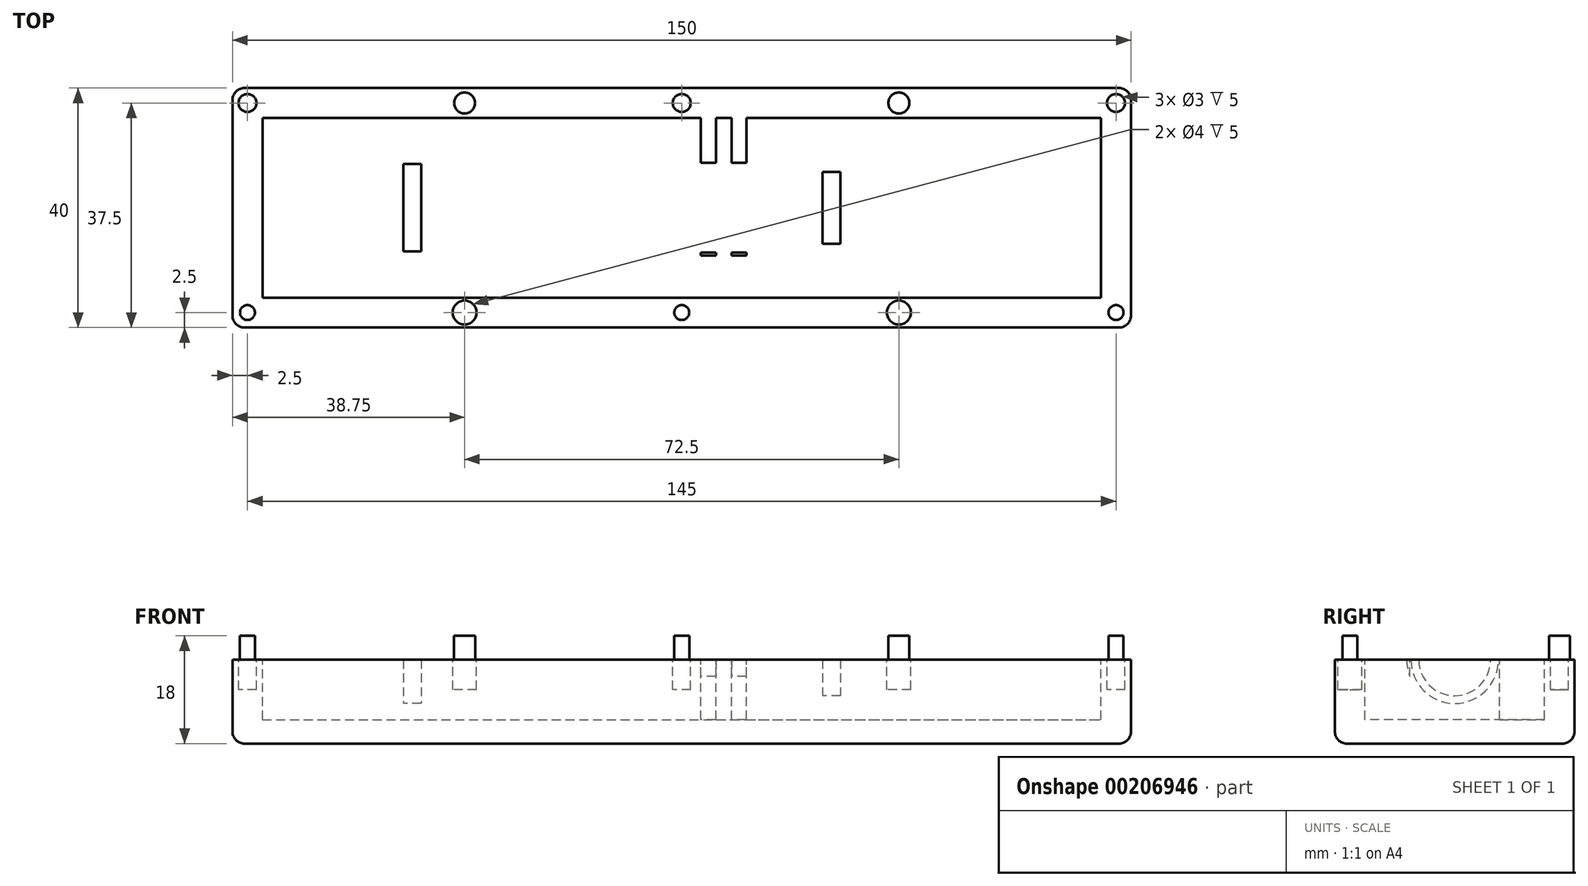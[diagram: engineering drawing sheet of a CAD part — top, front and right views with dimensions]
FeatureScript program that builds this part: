
annotation { "Feature Type Name" : "Feature", "Feature Type Description" : "" }
export const myFeature = defineFeature(function(context is Context, id is Id, definition is map)
    precondition{}
    {
        {
            var Q0;
            Q0=qCreatedBy(makeId("Top.planeOp"),FACE);
            var sketch = newSketch(context, id + "F0", { "sketchPlane" : qUnion([Q0])});
            skLineSegment(sketch, "E0.bottom", {"start": v(-70, 15) * mm, "end": v(70, 15) * mm});
            skLineSegment(sketch, "E0.top", {"start": v(-70, -15) * mm, "end": v(70, -15) * mm});
            skLineSegment(sketch, "E0.left", {"start": v(-70, 15) * mm, "end": v(-70, -15) * mm});
            skLineSegment(sketch, "E0.right", {"start": v(70, 15) * mm, "end": v(70, -15) * mm});
            skPoint(sketch, "E0.middle", {"position": v(0, 0) * mm});
            skLineSegment(sketch, "E1.bottom", {"start": v(3.2, 15) * mm, "end": v(10.8, 15) * mm});
            skLineSegment(sketch, "E1.top", {"start": v(3.2, -15) * mm, "end": v(10.8, -15) * mm});
            skLineSegment(sketch, "E1.left", {"start": v(3.2, 15) * mm, "end": v(3.2, -15) * mm});
            skLineSegment(sketch, "E1.right", {"start": v(10.8, 15) * mm, "end": v(10.8, -15) * mm});
            skPoint(sketch, "E1.middle", {"position": v(7, 0) * mm});
            skLineSegment(sketch, "E2.bottom", {"start": v(26.5, -8) * mm, "end": v(23.5, -8) * mm});
            skLineSegment(sketch, "E2.top", {"start": v(26.5, 8) * mm, "end": v(23.5, 8) * mm});
            skLineSegment(sketch, "E2.left", {"start": v(26.5, -8) * mm, "end": v(26.5, 8) * mm});
            skLineSegment(sketch, "E2.right", {"start": v(23.5, -8) * mm, "end": v(23.5, 8) * mm});
            skPoint(sketch, "E2.middle", {"position": v(25, 0) * mm});
            skPoint(sketch, "E2.middle.positionSnap0", {"position": v(10.8, 0) * mm});
            skLineSegment(sketch, "E3.bottom", {"start": v(-43.5, -8.5) * mm, "end": v(-46.5, -8.5) * mm});
            skLineSegment(sketch, "E3.top", {"start": v(-43.5, 8.5) * mm, "end": v(-46.5, 8.5) * mm});
            skLineSegment(sketch, "E3.left", {"start": v(-43.5, -8.5) * mm, "end": v(-43.5, 8.5) * mm});
            skLineSegment(sketch, "E3.right", {"start": v(-46.5, -8.5) * mm, "end": v(-46.5, 8.5) * mm});
            skPoint(sketch, "E3.middle", {"position": v(-45, 0) * mm});
            skLineSegment(sketch, "E4.0", {"start": v(-75, 20) * mm, "end": v(75, 20) * mm});
            skLineSegment(sketch, "E4.1", {"start": v(-75, 20) * mm, "end": v(-75, -20) * mm});
            skLineSegment(sketch, "E4.2", {"start": v(-75, -20) * mm, "end": v(75, -20) * mm});
            skLineSegment(sketch, "E4.3", {"start": v(75, 20) * mm, "end": v(75, -20) * mm});
            skLineSegment(sketch, "E5.bottom", {"start": v(26.5, -5) * mm, "end": v(23.5, -5) * mm});
            skLineSegment(sketch, "E5.top", {"start": v(26.5, 5) * mm, "end": v(23.5, 5) * mm});
            skLineSegment(sketch, "E5.left", {"start": v(26.5, -5) * mm, "end": v(26.5, 5) * mm});
            skLineSegment(sketch, "E5.right", {"start": v(23.5, -5) * mm, "end": v(23.5, 5) * mm});
            skLineSegment(sketch, "E6.bottom", {"start": v(-46.5, -7.5) * mm, "end": v(-43.5, -7.5) * mm});
            skLineSegment(sketch, "E6.top", {"start": v(-46.5, 7.5) * mm, "end": v(-43.5, 7.5) * mm});
            skLineSegment(sketch, "E6.left", {"start": v(-46.5, -7.5) * mm, "end": v(-46.5, 7.5) * mm});
            skLineSegment(sketch, "E6.right", {"start": v(-43.5, -7.5) * mm, "end": v(-43.5, 7.5) * mm});
            skLineSegment(sketch, "E7.bottom", {"start": v(10.8, -7.5) * mm, "end": v(3.2, -7.5) * mm});
            skLineSegment(sketch, "E7.top", {"start": v(10.8, 7.5) * mm, "end": v(3.2, 7.5) * mm});
            skLineSegment(sketch, "E7.left", {"start": v(10.8, -7.5) * mm, "end": v(10.8, 7.5) * mm});
            skLineSegment(sketch, "E7.right", {"start": v(3.2, -7.5) * mm, "end": v(3.2, 7.5) * mm});
            skLineSegment(sketch, "E8.bottom", {"start": v(8.3, -15) * mm, "end": v(5.7, -15) * mm});
            skLineSegment(sketch, "E8.top", {"start": v(8.3, 15) * mm, "end": v(5.7, 15) * mm});
            skLineSegment(sketch, "E8.left", {"start": v(8.3, -15) * mm, "end": v(8.3, 15) * mm});
            skLineSegment(sketch, "E8.right", {"start": v(5.7, -15) * mm, "end": v(5.7, 15) * mm});
            skLineSegment(sketch, "E9", {"start": v(-69, -15) * mm, "end": v(-69, -20) * mm, "construction": true});
            skLineSegment(sketch, "E10", {"start": v(-75, -17.5) * mm, "end": v(75, -17.5) * mm, "construction": true});
            skPoint(sketch, "E10.startSnap0", {"position": v(-69, -17.5) * mm});
            skLineSegment(sketch, "E11", {"start": v(70, -7.05) * mm, "end": v(75, -7.05) * mm, "construction": true});
            skLineSegment(sketch, "E12", {"start": v(72.5, -20) * mm, "end": v(72.5, 20) * mm, "construction": true});
            skPoint(sketch, "E12.startSnap0", {"position": v(72.5, -7.05) * mm});
            skLineSegment(sketch, "E13", {"start": v(68.1, 15) * mm, "end": v(68.1, 20) * mm, "construction": true});
            skLineSegment(sketch, "E14", {"start": v(75, 17.5) * mm, "end": v(-75, 17.5) * mm, "construction": true});
            skPoint(sketch, "E14.startSnap0", {"position": v(68.1, 17.5) * mm});
            skLineSegment(sketch, "E15", {"start": v(-75, 14.07) * mm, "end": v(-70, 14.07) * mm, "construction": true});
            skLineSegment(sketch, "E16", {"start": v(-72.5, 20) * mm, "end": v(-72.5, -20) * mm, "construction": true});
            skPoint(sketch, "E16.startSnap0", {"position": v(-72.5, 14.07) * mm});
            skCircle(sketch, "E17", {"center": v(-72.5, -17.5) * mm, "radius": 1.25 * mm});
            skLineSegment(sketch, "E18.direction1", {"start": v(-72.5, -17.5) * mm, "end": v(0, -17.5) * mm, "construction": true});
            skCircle(sketch, "E19.0.1.0", {"center": v(-72.5, 17.5) * mm, "radius": 1.5 * mm});
            skLineSegment(sketch, "E19.direction1", {"start": v(-72.5, -17.5) * mm, "end": v(-47.5, -17.5) * mm, "construction": true});
            skLineSegment(sketch, "E19.direction2", {"start": v(-72.5, -17.5) * mm, "end": v(-72.5, 17.5) * mm, "construction": true});
            skCircle(sketch, "E20.1.0.0", {"center": v(0, -17.5) * mm, "radius": 1.25 * mm});
            skCircle(sketch, "E20.2.0.0", {"center": v(72.5, -17.5) * mm, "radius": 1.25 * mm});
            skCircle(sketch, "E21.1.0.0", {"center": v(0, 17.5) * mm, "radius": 1.5 * mm});
            skCircle(sketch, "E21.2.0.0", {"center": v(72.5, 17.5) * mm, "radius": 1.5 * mm});
            skLineSegment(sketch, "E21.direction1", {"start": v(-72.5, 17.5) * mm, "end": v(0, 17.5) * mm, "construction": true});
            skCircle(sketch, "E22", {"center": v(-36.25, -17.5) * mm, "radius": 2 * mm});
            skCircle(sketch, "E23.0.1.0", {"center": v(-36.25, 17.5) * mm, "radius": 1.75 * mm});
            skCircle(sketch, "E23.1.0.0", {"center": v(36.25, -17.5) * mm, "radius": 2 * mm});
            skCircle(sketch, "E23.1.1.0", {"center": v(36.25, 17.5) * mm, "radius": 1.75 * mm});
            skLineSegment(sketch, "E23.direction1", {"start": v(-36.25, -17.5) * mm, "end": v(36.25, -17.5) * mm, "construction": true});
            skLineSegment(sketch, "E23.direction2", {"start": v(-36.25, -17.5) * mm, "end": v(-36.25, 17.5) * mm, "construction": true});
            skSolve(sketch);
        }
        {
            var Q0;
            {var subQ0=sQuery(id+"F0.wireOp",EDGE,"E3.top");Q0=makeQuery(id+"F0.imprint","IMPRINT",FACE,{"disambiguationData":[TD([[makeQuery(id+"F0.imprint","IMPRINT",EDGE,{"derivedFrom":subQ0}),1.0]])]});}
            var Q1;
            Q1=makeQuery(id+"F0.imprint","IMPRINT",FACE,{"disambiguationData":[TD([[makeQuery(id+"F0.imprint","IMPRINT",EDGE,{"derivedFrom":sQuery(id+"F0.wireOp",EDGE,"E6.bottom")}),1.0]])]});
            var Q2;
            {var subQ0=sQuery(id+"F0.wireOp",EDGE,"E3.bottom");Q2=makeQuery(id+"F0.imprint","IMPRINT",FACE,{"disambiguationData":[TD([[makeQuery(id+"F0.imprint","IMPRINT",EDGE,{"derivedFrom":subQ0}),-1.0]])]});}
            var Q3;
            {var subQ3=sQuery(id+"F0.wireOp",EDGE,"E8.right");var subQ5=sQuery(id+"F0.wireOp",EDGE,"E7.top");var subQ7=makeQuery(id+"F0.imprint","INTERSECT",VERTEX,{"derivedFrom":[subQ5,subQ3]});Q3=makeQuery(id+"F0.imprint","IMPRINT",FACE,{"disambiguationData":[TD([[makeQuery(id+"F0.imprint","IMPRINT",EDGE,{"disambiguationData":[TD([[subQ7,-1.0]])],"derivedFrom":subQ5}),-1.0]])]});}
            var Q4;
            {var subQ3=sQuery(id+"F0.wireOp",EDGE,"E8.left");var subQ5=sQuery(id+"F0.wireOp",EDGE,"E7.top");var subQ6=makeQuery(id+"F0.imprint","INTERSECT",VERTEX,{"derivedFrom":[subQ5,subQ3]});Q4=makeQuery(id+"F0.imprint","IMPRINT",FACE,{"disambiguationData":[TD([[makeQuery(id+"F0.imprint","IMPRINT",EDGE,{"disambiguationData":[TD([[subQ6,1.0]])],"derivedFrom":subQ5}),-1.0]])]});}
            var Q5;
            {var subQ0=sQuery(id+"F0.wireOp",EDGE,"E7.left");Q5=makeQuery(id+"F0.imprint","IMPRINT",FACE,{"disambiguationData":[TD([[makeQuery(id+"F0.imprint","IMPRINT",EDGE,{"derivedFrom":subQ0}),1.0]])]});}
            var Q6;
            {var subQ0=sQuery(id+"F0.wireOp",EDGE,"E7.right");Q6=makeQuery(id+"F0.imprint","IMPRINT",FACE,{"disambiguationData":[TD([[makeQuery(id+"F0.imprint","IMPRINT",EDGE,{"derivedFrom":subQ0}),-1.0]])]});}
            var Q7;
            {var subQ3=sQuery(id+"F0.wireOp",EDGE,"E8.right");var subQ5=sQuery(id+"F0.wireOp",EDGE,"E7.bottom");var subQ7=makeQuery(id+"F0.imprint","INTERSECT",VERTEX,{"derivedFrom":[subQ5,subQ3]});Q7=makeQuery(id+"F0.imprint","IMPRINT",FACE,{"disambiguationData":[TD([[makeQuery(id+"F0.imprint","IMPRINT",EDGE,{"disambiguationData":[TD([[subQ7,-1.0]])],"derivedFrom":subQ5}),1.0]])]});}
            var Q8;
            {var subQ3=sQuery(id+"F0.wireOp",EDGE,"E8.left");var subQ5=sQuery(id+"F0.wireOp",EDGE,"E7.bottom");var subQ7=makeQuery(id+"F0.imprint","INTERSECT",VERTEX,{"derivedFrom":[subQ5,subQ3]});Q8=makeQuery(id+"F0.imprint","IMPRINT",FACE,{"disambiguationData":[TD([[makeQuery(id+"F0.imprint","IMPRINT",EDGE,{"disambiguationData":[TD([[subQ7,1.0]])],"derivedFrom":subQ5}),1.0]])]});}
            var Q9;
            {var subQ0=sQuery(id+"F0.wireOp",EDGE,"E2.top");Q9=makeQuery(id+"F0.imprint","IMPRINT",FACE,{"disambiguationData":[TD([[makeQuery(id+"F0.imprint","IMPRINT",EDGE,{"derivedFrom":subQ0}),1.0]])]});}
            var Q10;
            Q10=makeQuery(id+"F0.imprint","IMPRINT",FACE,{"disambiguationData":[TD([[makeQuery(id+"F0.imprint","IMPRINT",EDGE,{"derivedFrom":sQuery(id+"F0.wireOp",EDGE,"E5.bottom")}),-1.0]])]});
            var Q11;
            {var subQ0=sQuery(id+"F0.wireOp",EDGE,"E2.bottom");Q11=makeQuery(id+"F0.imprint","IMPRINT",FACE,{"disambiguationData":[TD([[makeQuery(id+"F0.imprint","IMPRINT",EDGE,{"derivedFrom":subQ0}),-1.0]])]});}
            var Q12;
            {var subQ6=sQuery(id+"F0.wireOp",EDGE,"E0.left");Q12=makeQuery(id+"F0.imprint","IMPRINT",FACE,{"disambiguationData":[TD([[makeQuery(id+"F0.imprint","IMPRINT",EDGE,{"derivedFrom":subQ6}),-1.0]])]});}
            var Q13;
            Q13=makeQuery(id+"F0.imprint","IMPRINT",FACE,{"disambiguationData":[TD([[makeQuery(id+"F0.imprint","IMPRINT",EDGE,{"derivedFrom":sQuery(id+"F0.wireOp",EDGE,"E17")}),1.0]])]});
            var Q14;
            Q14=makeQuery(id+"F0.imprint","IMPRINT",FACE,{"disambiguationData":[TD([[makeQuery(id+"F0.imprint","IMPRINT",EDGE,{"derivedFrom":sQuery(id+"F0.wireOp",EDGE,"E20.1.0.0")}),1.0]])]});
            var Q15;
            Q15=makeQuery(id+"F0.imprint","IMPRINT",FACE,{"disambiguationData":[TD([[makeQuery(id+"F0.imprint","IMPRINT",EDGE,{"derivedFrom":sQuery(id+"F0.wireOp",EDGE,"E20.2.0.0")}),1.0]])]});
            var Q16;
            Q16=makeQuery(id+"F0.imprint","IMPRINT",FACE,{"disambiguationData":[TD([[makeQuery(id+"F0.imprint","IMPRINT",EDGE,{"derivedFrom":sQuery(id+"F0.wireOp",EDGE,"E21.2.0.0")}),1.0]])]});
            var Q17;
            Q17=makeQuery(id+"F0.imprint","IMPRINT",FACE,{"disambiguationData":[TD([[makeQuery(id+"F0.imprint","IMPRINT",EDGE,{"derivedFrom":sQuery(id+"F0.wireOp",EDGE,"E21.1.0.0")}),1.0]])]});
            var Q18;
            Q18=makeQuery(id+"F0.imprint","IMPRINT",FACE,{"disambiguationData":[TD([[makeQuery(id+"F0.imprint","IMPRINT",EDGE,{"derivedFrom":sQuery(id+"F0.wireOp",EDGE,"E19.0.1.0")}),1.0]])]});
            var Q19;
            Q19=makeQuery(id+"F0.imprint","IMPRINT",FACE,{"disambiguationData":[TD([[makeQuery(id+"F0.imprint","IMPRINT",EDGE,{"derivedFrom":sQuery(id+"F0.wireOp",EDGE,"E23.0.1.0")}),1.0]])]});
            var Q20;
            Q20=makeQuery(id+"F0.imprint","IMPRINT",FACE,{"disambiguationData":[TD([[makeQuery(id+"F0.imprint","IMPRINT",EDGE,{"derivedFrom":sQuery(id+"F0.wireOp",EDGE,"E23.1.1.0")}),1.0]])]});
            var Q21;
            Q21=makeQuery(id+"F0.imprint","IMPRINT",FACE,{"disambiguationData":[TD([[makeQuery(id+"F0.imprint","IMPRINT",EDGE,{"derivedFrom":sQuery(id+"F0.wireOp",EDGE,"E22")}),1.0]])]});
            var Q22;
            Q22=makeQuery(id+"F0.imprint","IMPRINT",FACE,{"disambiguationData":[TD([[makeQuery(id+"F0.imprint","IMPRINT",EDGE,{"derivedFrom":sQuery(id+"F0.wireOp",EDGE,"E23.1.0.0")}),1.0]])]});
            extrude(context, id + "F1", {"entities" : qUnion([Q0, Q1, Q2, Q3, Q4, Q5, Q6, Q7, Q8, Q9, Q10, Q11, Q12, Q13, Q14, Q15, Q16, Q17, Q18, Q19, Q20, Q21, Q22]), "oppositeDirection" : true, "depth" : 10 * mm});
        }
        {
            var Q0;
            Q0=makeQuery(id+"F1.opExtrude","SWEPT_FACE",FACE,{"disambiguationData":[OSD([sQuery(id+"F0.wireOp",EDGE,"E3.right"),sQuery(id+"F0.wireOp",EDGE,"E6.left")])]});
            var sketch = newSketch(context, id + "F2", { "sketchPlane" : qUnion([Q0])});
            skArc(sketch, "E24", {"start": v(7.3, 0) * mm, "mid": v(0, -7.3) * mm, "end": v(-7.3, 0) * mm});
            skSolve(sketch);
        }
        {
            var Q0;
            {var subQ0=sQuery(id+"F2.wireOp",EDGE,"E24");Q0=makeQuery(id+"F2.imprint","IMPRINT",FACE,{"disambiguationData":[TD([[makeQuery(id+"F2.imprint","IMPRINT",EDGE,{"derivedFrom":subQ0}),-1.0]])]});}
            extrude(context, id + "F3", {"entities" : qUnion([Q0]), "operationType" : NewBodyOperationType.REMOVE, "endBound" : BoundingType.UP_TO_NEXT, "oppositeDirection" : true, "depth" : 25 * mm});
        }
        {
            var Q0;
            Q0=makeQuery(id+"F1.opExtrude","SWEPT_FACE",FACE,{"disambiguationData":[OSD([sQuery(id+"F0.wireOp",EDGE,"E1.left"),sQuery(id+"F0.wireOp",EDGE,"E7.right")])]});
            var sketch = newSketch(context, id + "F4", { "sketchPlane" : qUnion([Q0])});
            skArc(sketch, "E25", {"start": v(8, 0) * mm, "mid": v(0, -8) * mm, "end": v(-8, 0) * mm});
            skSolve(sketch);
        }
        {
            var Q0;
            {var subQ0=sQuery(id+"F4.wireOp",EDGE,"E25");Q0=makeQuery(id+"F4.imprint","IMPRINT",FACE,{"disambiguationData":[TD([[makeQuery(id+"F4.imprint","IMPRINT",EDGE,{"derivedFrom":subQ0}),-1.0]])]});}
            var Q1;
            Q1=makeQuery(id+"F1.opExtrude","SWEPT_FACE",FACE,{"disambiguationData":[OSD([sQuery(id+"F0.wireOp",EDGE,"E1.right"),sQuery(id+"F0.wireOp",EDGE,"E7.left")])]});
            extrude(context, id + "F5", {"entities" : qUnion([Q0]), "operationType" : NewBodyOperationType.REMOVE, "endBound" : BoundingType.UP_TO_SURFACE, "oppositeDirection" : true, "endBoundEntityFace" : qUnion([Q1]), "depth" : 25 * mm});
        }
        {
            var Q0;
            Q0=makeQuery(id+"F1.opExtrude","SWEPT_FACE",FACE,{"disambiguationData":[OSD([sQuery(id+"F0.wireOp",EDGE,"E2.right"),sQuery(id+"F0.wireOp",EDGE,"E5.right")])]});
            var sketch = newSketch(context, id + "F6", { "sketchPlane" : qUnion([Q0])});
            skArc(sketch, "E26", {"start": v(6, 0) * mm, "mid": v(0, -6) * mm, "end": v(-6, 0) * mm});
            skSolve(sketch);
        }
        {
            var Q0;
            {var subQ0=sQuery(id+"F6.wireOp",EDGE,"E26");Q0=makeQuery(id+"F6.imprint","IMPRINT",FACE,{"disambiguationData":[TD([[makeQuery(id+"F6.imprint","IMPRINT",EDGE,{"derivedFrom":subQ0}),-1.0]])]});}
            extrude(context, id + "F7", {"entities" : qUnion([Q0]), "operationType" : NewBodyOperationType.REMOVE, "endBound" : BoundingType.UP_TO_NEXT, "oppositeDirection" : true, "depth" : 25 * mm});
        }
        {
            var Q0;
            Q0=makeQuery(id+"F0.imprint","IMPRINT",FACE,{"disambiguationData":[TD([[makeQuery(id+"F0.imprint","IMPRINT",EDGE,{"derivedFrom":sQuery(id+"F0.wireOp",EDGE,"E17")}),1.0]])]});
            var Q1;
            Q1=makeQuery(id+"F0.imprint","IMPRINT",FACE,{"disambiguationData":[TD([[makeQuery(id+"F0.imprint","IMPRINT",EDGE,{"derivedFrom":sQuery(id+"F0.wireOp",EDGE,"E20.1.0.0")}),1.0]])]});
            var Q2;
            Q2=makeQuery(id+"F0.imprint","IMPRINT",FACE,{"disambiguationData":[TD([[makeQuery(id+"F0.imprint","IMPRINT",EDGE,{"derivedFrom":sQuery(id+"F0.wireOp",EDGE,"E20.2.0.0")}),1.0]])]});
            var Q3;
            Q3=makeQuery(id+"F0.imprint","IMPRINT",FACE,{"disambiguationData":[TD([[makeQuery(id+"F0.imprint","IMPRINT",EDGE,{"derivedFrom":sQuery(id+"F0.wireOp",EDGE,"E23.0.1.0")}),1.0]])]});
            var Q4;
            Q4=makeQuery(id+"F0.imprint","IMPRINT",FACE,{"disambiguationData":[TD([[makeQuery(id+"F0.imprint","IMPRINT",EDGE,{"derivedFrom":sQuery(id+"F0.wireOp",EDGE,"E23.1.1.0")}),1.0]])]});
            extrude(context, id + "F8", {"entities" : qUnion([Q0, Q1, Q2, Q3, Q4]), "operationType" : NewBodyOperationType.ADD, "depth" : 4 * mm});
        }
        {
            var Q0;
            Q0=makeQuery(id+"F0.imprint","IMPRINT",FACE,{"disambiguationData":[TD([[makeQuery(id+"F0.imprint","IMPRINT",EDGE,{"derivedFrom":sQuery(id+"F0.wireOp",EDGE,"E21.1.0.0")}),1.0]])]});
            var Q1;
            Q1=makeQuery(id+"F0.imprint","IMPRINT",FACE,{"disambiguationData":[TD([[makeQuery(id+"F0.imprint","IMPRINT",EDGE,{"derivedFrom":sQuery(id+"F0.wireOp",EDGE,"E21.2.0.0")}),1.0]])]});
            var Q2;
            Q2=makeQuery(id+"F0.imprint","IMPRINT",FACE,{"disambiguationData":[TD([[makeQuery(id+"F0.imprint","IMPRINT",EDGE,{"derivedFrom":sQuery(id+"F0.wireOp",EDGE,"E19.0.1.0")}),1.0]])]});
            var Q3;
            Q3=makeQuery(id+"F0.imprint","IMPRINT",FACE,{"disambiguationData":[TD([[makeQuery(id+"F0.imprint","IMPRINT",EDGE,{"derivedFrom":sQuery(id+"F0.wireOp",EDGE,"E22")}),1.0]])]});
            var Q4;
            Q4=makeQuery(id+"F0.imprint","IMPRINT",FACE,{"disambiguationData":[TD([[makeQuery(id+"F0.imprint","IMPRINT",EDGE,{"derivedFrom":sQuery(id+"F0.wireOp",EDGE,"E23.1.0.0")}),1.0]])]});
            extrude(context, id + "F9", {"entities" : qUnion([Q0, Q1, Q2, Q3, Q4]), "operationType" : NewBodyOperationType.REMOVE, "oppositeDirection" : true, "depth" : 5 * mm});
        }
        {
            var Q0;
            Q0=makeQuery(id+"F1.opExtrude","CAP_FACE",FACE,{"disambiguationData":[OSD([sQuery(id+"F0.wireOp",EDGE,"E0.bottom"),sQuery(id+"F0.wireOp",EDGE,"E0.top"),sQuery(id+"F0.wireOp",EDGE,"E0.left"),sQuery(id+"F0.wireOp",EDGE,"E0.right"),sQuery(id+"F0.wireOp",EDGE,"E1.left"),sQuery(id+"F0.wireOp",EDGE,"E1.right"),sQuery(id+"F0.wireOp",EDGE,"E4.0"),sQuery(id+"F0.wireOp",EDGE,"E4.1"),sQuery(id+"F0.wireOp",EDGE,"E4.2"),sQuery(id+"F0.wireOp",EDGE,"E4.3"),sQuery(id+"F0.wireOp",EDGE,"E7.left"),sQuery(id+"F0.wireOp",EDGE,"E7.right"),sQuery(id+"F0.wireOp",EDGE,"E8.bottom"),sQuery(id+"F0.wireOp",EDGE,"E8.top"),sQuery(id+"F0.wireOp",EDGE,"E8.left"),sQuery(id+"F0.wireOp",EDGE,"E8.right")])],"isStart":false});
            var sketch = newSketch(context, id + "F10", { "sketchPlane" : qUnion([Q0])});
            skLineSegment(sketch, "E27.bottom", {"start": v(-75, 20) * mm, "end": v(75, 20) * mm});
            skLineSegment(sketch, "E27.top", {"start": v(-75, -20) * mm, "end": v(75, -20) * mm});
            skLineSegment(sketch, "E27.left", {"start": v(-75, 20) * mm, "end": v(-75, -20) * mm});
            skLineSegment(sketch, "E27.right", {"start": v(75, 20) * mm, "end": v(75, -20) * mm});
            skSolve(sketch);
        }
        {
            var Q0;
            {var subQ0=sQuery(id+"F0.wireOp",EDGE,"E0.left");Q0=makeQuery(id+"F10.imprint","IMPRINT",FACE,{"disambiguationData":[TD([[makeQuery(id+"F10.imprint","IMPRINT",EDGE,{"derivedFrom":makeQuery(id+"F1.opExtrude","CAP_EDGE",EDGE,{"disambiguationData":[OSD([subQ0])],"isStart":false})}),-1.0]])]});}
            var Q1;
            {var subQ0=sQuery(id+"F0.wireOp",EDGE,"E0.right");Q1=makeQuery(id+"F10.imprint","IMPRINT",FACE,{"disambiguationData":[TD([[makeQuery(id+"F10.imprint","IMPRINT",EDGE,{"derivedFrom":makeQuery(id+"F1.opExtrude","CAP_EDGE",EDGE,{"disambiguationData":[OSD([subQ0])],"isStart":false})}),1.0]])]});}
            var Q2;
            Q2=makeQuery(id+"F10.imprint","IMPRINT",FACE,{"disambiguationData":[TD([[makeQuery(id+"F10.imprint","IMPRINT",EDGE,{"derivedFrom":sQuery(id+"F10.wireOp",EDGE,"E27.bottom")}),-1.0]])]});
            var Q3;
            Q3=makeQuery(id+"F10.imprint","IMPRINT",FACE,{"disambiguationData":[TD([[makeQuery(id+"F10.imprint","IMPRINT",EDGE,{"derivedFrom":makeQuery(id+"F1.opExtrude","CAP_EDGE",EDGE,{"disambiguationData":[OSD([sQuery(id+"F0.wireOp",EDGE,"E8.bottom")])],"isStart":false})}),1.0]])]});
            extrude(context, id + "F11", {"entities" : qUnion([Q0, Q1, Q2, Q3]), "depth" : 4 * mm});
        }
        {
            var Q0;
            Q0=makeQuery(id+"F11.opExtrude","SWEPT_BODY",BODY,{"disambiguationData":[OSD([sQuery(id+"F10.wireOp",EDGE,"E27.bottom"),sQuery(id+"F10.wireOp",EDGE,"E27.top"),sQuery(id+"F10.wireOp",EDGE,"E27.left"),sQuery(id+"F10.wireOp",EDGE,"E27.right")])]});
            var Q1;
            Q1=makeQuery(id+"F1.opExtrude","SWEPT_BODY",BODY,{"disambiguationData":[OSD([sQuery(id+"F0.wireOp",EDGE,"E2.bottom"),sQuery(id+"F0.wireOp",EDGE,"E2.top"),sQuery(id+"F0.wireOp",EDGE,"E2.left"),sQuery(id+"F0.wireOp",EDGE,"E2.right"),sQuery(id+"F0.wireOp",EDGE,"E5.left"),sQuery(id+"F0.wireOp",EDGE,"E5.right")])]});
            var Q2;
            Q2=makeQuery(id+"F1.opExtrude","SWEPT_BODY",BODY,{"disambiguationData":[OSD([sQuery(id+"F0.wireOp",EDGE,"E0.bottom"),sQuery(id+"F0.wireOp",EDGE,"E0.top"),sQuery(id+"F0.wireOp",EDGE,"E0.left"),sQuery(id+"F0.wireOp",EDGE,"E0.right"),sQuery(id+"F0.wireOp",EDGE,"E1.left"),sQuery(id+"F0.wireOp",EDGE,"E1.right"),sQuery(id+"F0.wireOp",EDGE,"E4.0"),sQuery(id+"F0.wireOp",EDGE,"E4.1"),sQuery(id+"F0.wireOp",EDGE,"E4.2"),sQuery(id+"F0.wireOp",EDGE,"E4.3"),sQuery(id+"F0.wireOp",EDGE,"E7.left"),sQuery(id+"F0.wireOp",EDGE,"E7.right"),sQuery(id+"F0.wireOp",EDGE,"E8.bottom"),sQuery(id+"F0.wireOp",EDGE,"E8.top"),sQuery(id+"F0.wireOp",EDGE,"E8.left"),sQuery(id+"F0.wireOp",EDGE,"E8.right")])]});
            var Q3;
            Q3=makeQuery(id+"F1.opExtrude","SWEPT_BODY",BODY,{"disambiguationData":[OSD([sQuery(id+"F0.wireOp",EDGE,"E3.bottom"),sQuery(id+"F0.wireOp",EDGE,"E3.top"),sQuery(id+"F0.wireOp",EDGE,"E3.left"),sQuery(id+"F0.wireOp",EDGE,"E3.right"),sQuery(id+"F0.wireOp",EDGE,"E6.left"),sQuery(id+"F0.wireOp",EDGE,"E6.right")])]});
            booleanBodies(context, id + "F12", {"operationType" : BooleanOperationType.UNION, "tools" : qUnion([Q0, Q1, Q2, Q3])});
        }
        {
            var Q0;
            Q0=makeQuery(id+"F12.opBoolean","MERGE",EDGE,{"derivedFrom":[makeQuery(id+"F1.opExtrude","SWEPT_EDGE",EDGE,{"disambiguationData":[OSD([sQuery(id+"F0.wireOp",EDGE,"E4.1"),sQuery(id+"F0.wireOp",EDGE,"E4.2")])]}),makeQuery(id+"F11.opExtrude","SWEPT_EDGE",EDGE,{"disambiguationData":[OSD([sQuery(id+"F10.wireOp",EDGE,"E27.bottom"),sQuery(id+"F10.wireOp",EDGE,"E27.left")])]})]});
            var Q1;
            Q1=makeQuery(id+"F12.opBoolean","MERGE",EDGE,{"derivedFrom":[makeQuery(id+"F1.opExtrude","SWEPT_EDGE",EDGE,{"disambiguationData":[OSD([sQuery(id+"F0.wireOp",EDGE,"E4.2"),sQuery(id+"F0.wireOp",EDGE,"E4.3")])]}),makeQuery(id+"F11.opExtrude","SWEPT_EDGE",EDGE,{"disambiguationData":[OSD([sQuery(id+"F10.wireOp",EDGE,"E27.bottom"),sQuery(id+"F10.wireOp",EDGE,"E27.right")])]})]});
            var Q2;
            Q2=makeQuery(id+"F12.opBoolean","MERGE",EDGE,{"derivedFrom":[makeQuery(id+"F1.opExtrude","SWEPT_EDGE",EDGE,{"disambiguationData":[OSD([sQuery(id+"F0.wireOp",EDGE,"E4.0"),sQuery(id+"F0.wireOp",EDGE,"E4.3")])]}),makeQuery(id+"F11.opExtrude","SWEPT_EDGE",EDGE,{"disambiguationData":[OSD([sQuery(id+"F10.wireOp",EDGE,"E27.top"),sQuery(id+"F10.wireOp",EDGE,"E27.right")])]})]});
            var Q3;
            Q3=makeQuery(id+"F12.opBoolean","MERGE",EDGE,{"derivedFrom":[makeQuery(id+"F1.opExtrude","SWEPT_EDGE",EDGE,{"disambiguationData":[OSD([sQuery(id+"F0.wireOp",EDGE,"E4.0"),sQuery(id+"F0.wireOp",EDGE,"E4.1")])]}),makeQuery(id+"F11.opExtrude","SWEPT_EDGE",EDGE,{"disambiguationData":[OSD([sQuery(id+"F10.wireOp",EDGE,"E27.top"),sQuery(id+"F10.wireOp",EDGE,"E27.left")])]})]});
            var Q4;
            Q4=makeQuery(id+"F11.opExtrude","CAP_EDGE",EDGE,{"disambiguationData":[OSD([sQuery(id+"F10.wireOp",EDGE,"E27.left")])],"isStart":false});
            var Q5;
            Q5=makeQuery(id+"F11.opExtrude","CAP_EDGE",EDGE,{"disambiguationData":[OSD([sQuery(id+"F10.wireOp",EDGE,"E27.bottom")])],"isStart":false});
            var Q6;
            Q6=makeQuery(id+"F11.opExtrude","CAP_EDGE",EDGE,{"disambiguationData":[OSD([sQuery(id+"F10.wireOp",EDGE,"E27.top")])],"isStart":false});
            var Q7;
            Q7=makeQuery(id+"F11.opExtrude","CAP_EDGE",EDGE,{"disambiguationData":[OSD([sQuery(id+"F10.wireOp",EDGE,"E27.right")])],"isStart":false});
            fillet(context, id + "F13", {"entities" : qUnion([Q0, Q1, Q2, Q3, Q4, Q5, Q6, Q7]), "radius" : 2 * mm, "tangentPropagation" : true, "allowEdgeOverflow" : false});
        }
    });
